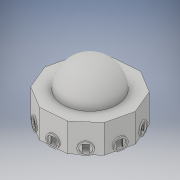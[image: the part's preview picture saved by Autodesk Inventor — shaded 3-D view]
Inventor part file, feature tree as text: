
AUTODESK INVENTOR PART (.ipt)
format: ipt  version: 2017 (Build 210142000, 142)  size: 446,464 bytes
history: native  units: in
note: dims shown in document units (in); Inventor stores cm internally (conversion verified against a paired STEP export)
features: sketch x7, extrude x6, other x3, mirror x1, pattern_circular x1
ambient origin geometry x8: Origin, YZ Plane, XZ Plane, XY Plane, X Axis, Y Axis, Z Axis, Center Point
bodies: Solid1 (feature_tree)
feature tree (18):
  extrude  "bace"  Depth=1.0in TaperAngle=0.0deg
  extrude  "bace wall"  Depth=20.0in TaperAngle=0.0deg
  extrude  "bace cieiling"  Depth=6.6667in
  other  "dome work plane"
  other  "dome"
  extrude  "door frame"  Depth=1.0in TaperAngle=0.0deg
  extrude  "corridor connection"  Depth=0.25in
  extrude  "left door slot"  Depth=2.0in
  other  "door slot mirror"
  mirror  "other side of the door"
  pattern_circular  "Circular Pattern1"  [2 undecoded]
  sketch  "Sketch1"  dims[d0=62.0in d1=1.0in d2=0.0in]
  sketch  "Sketch2"  dims[d4=1.0in d5=20.0in d6=0.0in]
  sketch  "Sketch3"  dims[d8=1.0in d9=0.0in d14=6.6667in d15=4.0in]
  sketch  "Sketch7"  dims[d16=2.0in d17=6.6667in d18=1.0in d19=0.0in]
  sketch  "Sketch8"  dims[d20=1.0in d21=0.0in d22=0.25in d23=0.5in d24=6.6667in]
  sketch  "Sketch9"  dims[d25=2.0in d26=0.0in d28=40.0in]
  sketch  "Sketch10"  dims[d32=20.0in d33=21.0in d34=90.0deg d35=3.937in d36=360.0deg]
note: 2 required parameter values undecoded (feature->parameter linkage not recoverable at this tier; creation-order binding heuristic only, values carry confidence <= 0.55)
